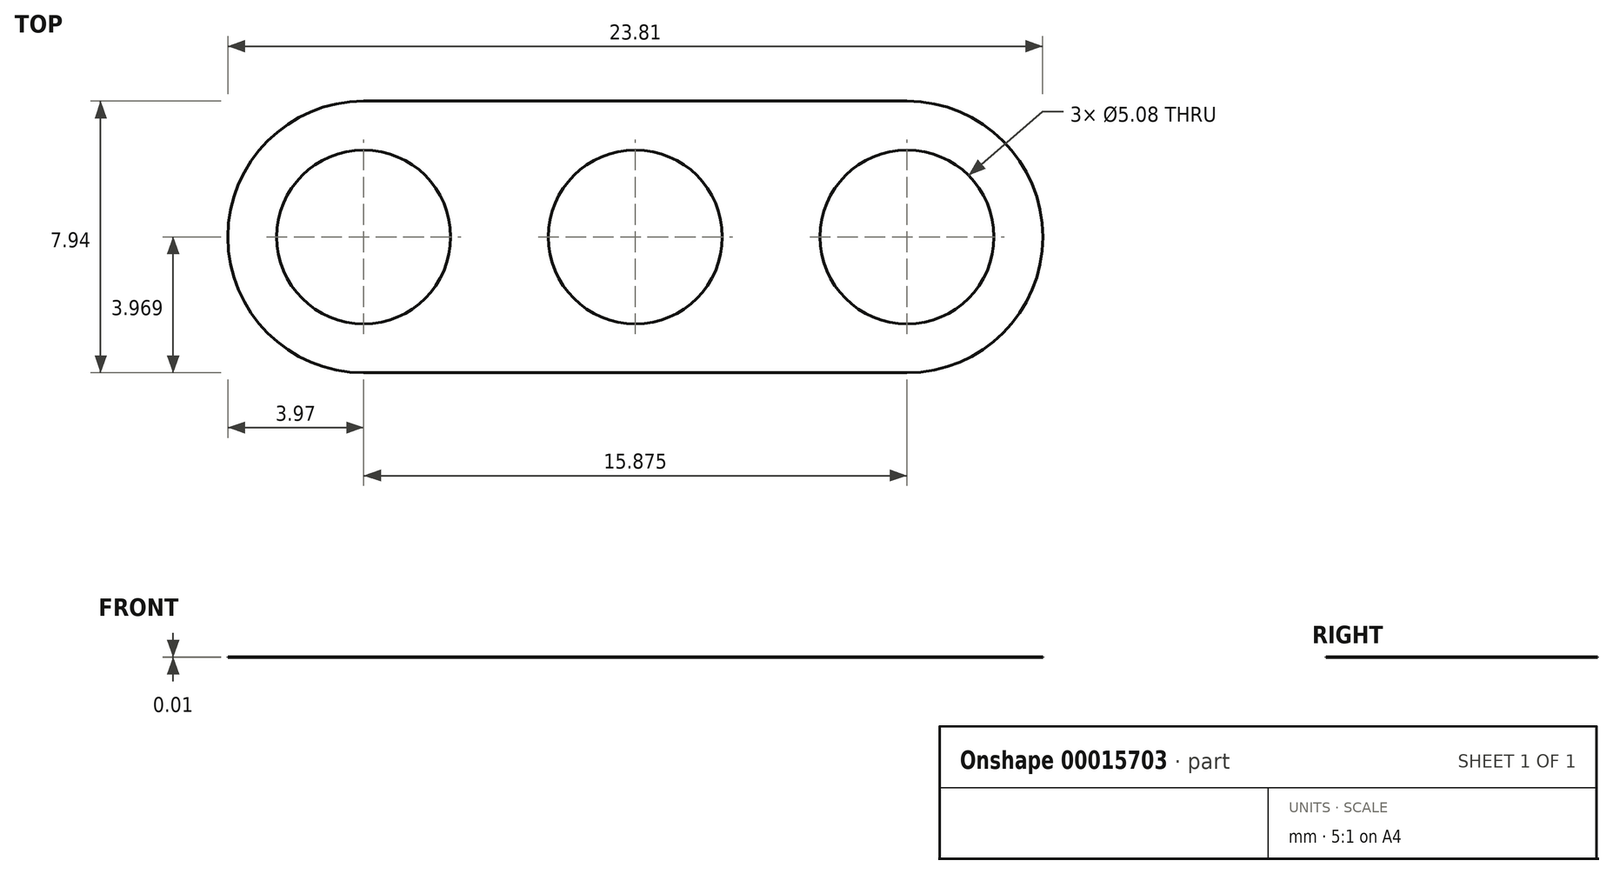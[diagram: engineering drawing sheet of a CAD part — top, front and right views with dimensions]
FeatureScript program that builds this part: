
annotation { "Feature Type Name" : "Feature", "Feature Type Description" : "" }
export const myFeature = defineFeature(function(context is Context, id is Id, definition is map)
    precondition{}
    {
        {
            var Q0;
            Q0=qCreatedBy(makeId("Top.planeOp"),FACE);
            var sketch = newSketch(context, id + "F0", { "sketchPlane" : qUnion([Q0])});
            skLineSegment(sketch, "E0.bottom", {"start": v(0, 0) * mm, "end": v(15.88, 0) * mm});
            skLineSegment(sketch, "E0.top", {"start": v(0, 7.94) * mm, "end": v(15.88, 7.94) * mm});
            skLineSegment(sketch, "E0.left", {"start": v(0, 0) * mm, "end": v(0, 7.94) * mm});
            skLineSegment(sketch, "E0.right", {"start": v(15.88, 0) * mm, "end": v(15.88, 7.94) * mm});
            skLineSegment(sketch, "E1", {"start": v(7.94, 3.97) * mm, "end": v(15.88, 3.97) * mm});
            skCircle(sketch, "E2", {"center": v(15.88, 3.97) * mm, "radius": 2.54 * mm});
            skCircle(sketch, "E3", {"center": v(7.94, 3.97) * mm, "radius": 2.54 * mm});
            skCircle(sketch, "E4", {"center": v(0, 3.97) * mm, "radius": 2.54 * mm});
            skLineSegment(sketch, "E5", {"start": v(7.94, 3.97) * mm, "end": v(0, 3.97) * mm});
            skArc(sketch, "E6", {"start": v(15.88, 0) * mm, "mid": v(19.84, 3.97) * mm, "end": v(15.88, 7.94) * mm});
            skArc(sketch, "E7", {"start": v(0, 7.94) * mm, "mid": v(-3.97, 3.97) * mm, "end": v(0, 0) * mm});
            skSolve(sketch);
        }
        {
            var Q0;
            Q0=qSketchRegion(id+"F0",true);
            extrude(context, id + "F1", {"entities" : qUnion([Q0]), "depth" : 5 / 406.4 * mm});
        }
    });
